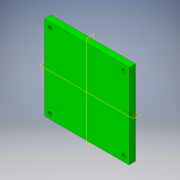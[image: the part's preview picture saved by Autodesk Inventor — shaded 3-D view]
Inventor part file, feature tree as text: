
AUTODESK INVENTOR PART (.ipt)
format: ipt  version: 2016 (Build 200138000, 138)  size: 131,584 bytes
history: native  units: in
note: dims shown in document units (in); Inventor stores cm internally (conversion verified against a paired STEP export)
features: plane x2, extrude x1, sketch x1, other x1
ambient origin geometry x8: Origin, YZ Plane, XZ Plane, XY Plane, X Axis, Y Axis, Z Axis, Center Point
bodies: Solid1 (feature_tree)
feature tree (5):
  plane  "Work Plane1"
  plane  "Work Plane2"
  extrude  "Extrusion1"  [1 undecoded]
  sketch  "Sketch1"  dims[d0=0.3937in d1=0.0in]
  other  "Formsenkung für M8 Linsensenkschraube1"
note: 1 required parameter value undecoded (feature->parameter linkage not recoverable at this tier; creation-order binding heuristic only, values carry confidence <= 0.55)
